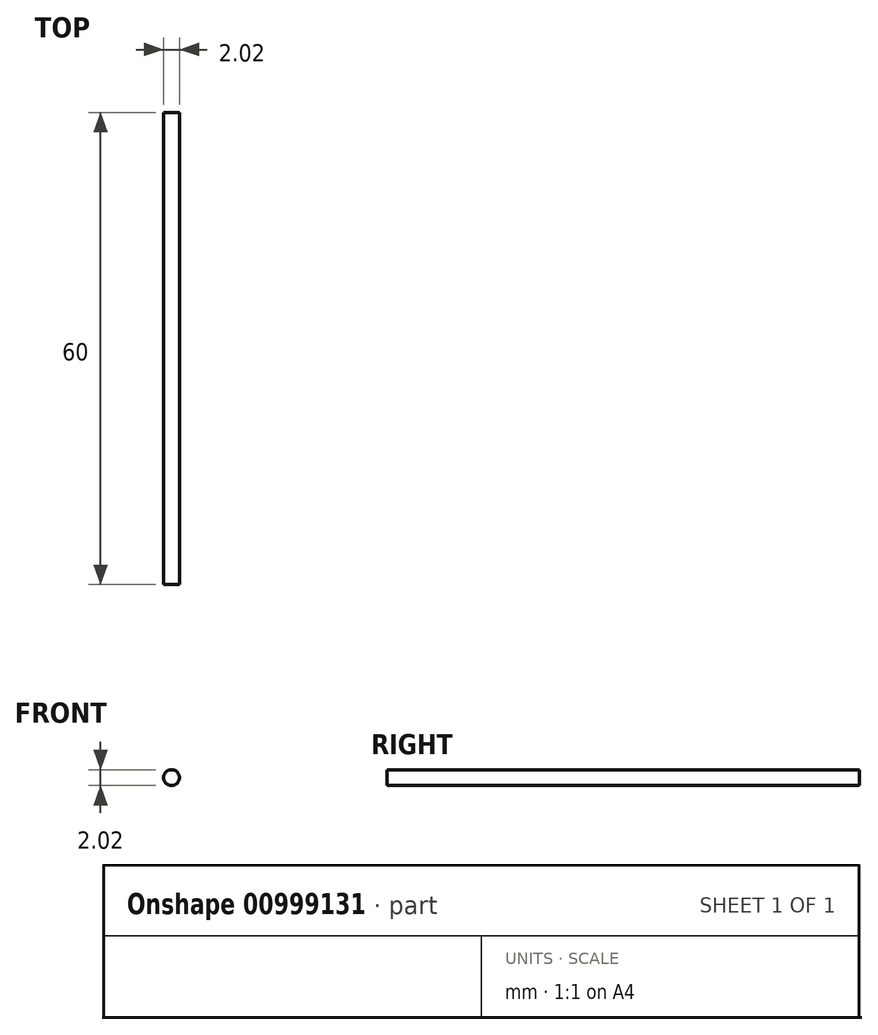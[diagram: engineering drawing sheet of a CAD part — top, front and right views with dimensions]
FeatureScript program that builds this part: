
annotation { "Feature Type Name" : "Feature", "Feature Type Description" : "" }
export const myFeature = defineFeature(function(context is Context, id is Id, definition is map)
    precondition{}
    {
        {
            var Q0;
            Q0=qCreatedBy(makeId("Front.planeOp"),FACE);
            var sketch = newSketch(context, id + "F0", { "sketchPlane" : qUnion([Q0])});
            skCircle(sketch, "E0", {"center": v(0, 0) * mm, "radius": 1.01 * mm});
            skPoint(sketch, "E1", {"position": v(1, 0.14) * mm});
            skSolve(sketch);
        }
        {
            var Q0;
            Q0 = qSketchRegion(id + "F0", true);
            extrude(context, id + "F1", {"entities" : qUnion([Q0]), "depth" : 60 * mm, "offsetDistance" : 25 * mm});
        }
    });
